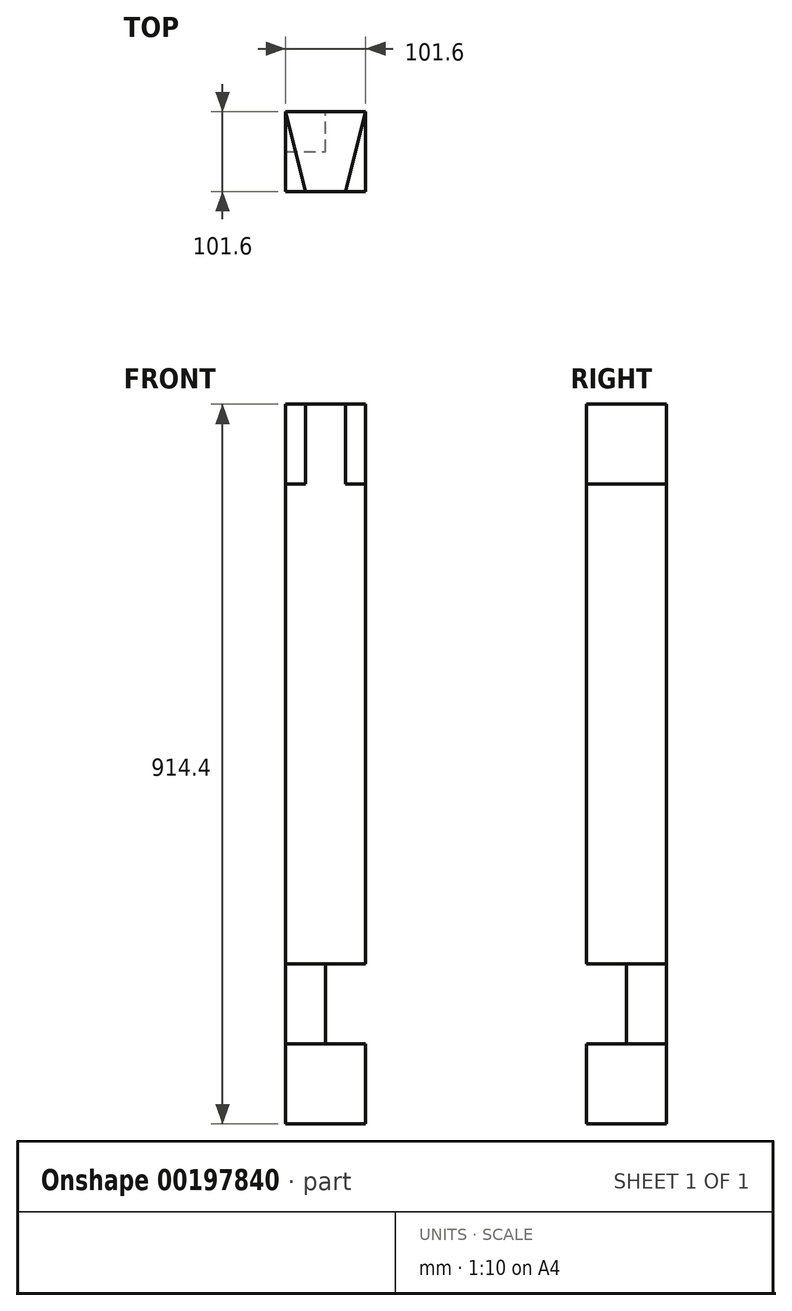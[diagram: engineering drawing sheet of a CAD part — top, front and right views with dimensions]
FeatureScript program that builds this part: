
annotation { "Feature Type Name" : "Feature", "Feature Type Description" : "" }
export const myFeature = defineFeature(function(context is Context, id is Id, definition is map)
    precondition{}
    {
        {
            var Q0;
            Q0=qCreatedBy(makeId("Top.planeOp"),FACE);
            var sketch = newSketch(context, id + "F0", { "sketchPlane" : qUnion([Q0])});
            skLineSegment(sketch, "E0.bottom", {"start": v(50.8, -50.8) * mm, "end": v(-50.8, -50.8) * mm});
            skLineSegment(sketch, "E0.top", {"start": v(50.8, 50.8) * mm, "end": v(-50.8, 50.8) * mm});
            skLineSegment(sketch, "E0.left", {"start": v(50.8, -50.8) * mm, "end": v(50.8, 50.8) * mm});
            skLineSegment(sketch, "E0.right", {"start": v(-50.8, -50.8) * mm, "end": v(-50.8, 50.8) * mm});
            skPoint(sketch, "E0.middle", {"position": v(0, 0) * mm});
            skSolve(sketch);
        }
        {
            var Q0;
            Q0=makeQuery(id+"F0.imprint","IMPRINT",FACE,{"disambiguationData":[TD([[makeQuery(id+"F0.imprint","IMPRINT",EDGE,{"derivedFrom":sQuery(id+"F0.wireOp",EDGE,"E0.bottom")}),-1.0]])]});
            extrude(context, id + "F1", {"entities" : qUnion([Q0]), "depth" : 914.4 * mm});
        }
        {
            var Q0;
            Q0=makeQuery(id+"F1.opExtrude","CAP_FACE",FACE,{"disambiguationData":[OSD([sQuery(id+"F0.wireOp",EDGE,"E0.bottom"),sQuery(id+"F0.wireOp",EDGE,"E0.top"),sQuery(id+"F0.wireOp",EDGE,"E0.left"),sQuery(id+"F0.wireOp",EDGE,"E0.right")])],"isStart":false});
            var sketch = newSketch(context, id + "F2", { "sketchPlane" : qUnion([Q0])});
            skLineSegment(sketch, "E1", {"start": v(-50.8, 50.8) * mm, "end": v(-25.4, -50.8) * mm});
            skLineSegment(sketch, "E2", {"start": v(0, 50.8) * mm, "end": v(0, -50.8) * mm, "construction": true});
            skLineSegment(sketch, "E3.MirrorCS", {"start": v(50.8, 50.8) * mm, "end": v(25.4, -50.8) * mm});
            skLineSegment(sketch, "E4", {"start": v(-50.8, 50.8) * mm, "end": v(50.8, 50.8) * mm});
            skLineSegment(sketch, "E5", {"start": v(25.4, -50.8) * mm, "end": v(-25.4, -50.8) * mm});
            skSolve(sketch);
        }
        {
            var Q0;
            {var subQ0=sQuery(id+"F2.wireOp",EDGE,"E1");Q0=makeQuery(id+"F2.imprint","IMPRINT",FACE,{"disambiguationData":[TD([[makeQuery(id+"F2.imprint","IMPRINT",EDGE,{"derivedFrom":subQ0}),-1.0]])]});}
            var Q1;
            {var subQ0=sQuery(id+"F2.wireOp",EDGE,"E3.MirrorCS");Q1=makeQuery(id+"F2.imprint","IMPRINT",FACE,{"disambiguationData":[TD([[makeQuery(id+"F2.imprint","IMPRINT",EDGE,{"derivedFrom":subQ0}),1.0]])]});}
            extrude(context, id + "F3", {"entities" : qUnion([Q0, Q1]), "operationType" : NewBodyOperationType.REMOVE, "oppositeDirection" : true, "depth" : 101.6 * mm});
        }
        {
            var Q0;
            Q0=makeQuery(id+"F1.opExtrude","SWEPT_FACE",FACE,{"disambiguationData":[OSD([sQuery(id+"F0.wireOp",EDGE,"E0.bottom")])]});
            var sketch = newSketch(context, id + "F4", { "sketchPlane" : qUnion([Q0])});
            skLineSegment(sketch, "E6.bottom", {"start": v(-50.8, 203.2) * mm, "end": v(50.8, 203.2) * mm});
            skLineSegment(sketch, "E6.top", {"start": v(-50.8, 101.6) * mm, "end": v(50.8, 101.6) * mm});
            skLineSegment(sketch, "E6.left", {"start": v(-50.8, 203.2) * mm, "end": v(-50.8, 101.6) * mm});
            skLineSegment(sketch, "E6.right", {"start": v(50.8, 203.2) * mm, "end": v(50.8, 101.6) * mm});
            skSolve(sketch);
        }
        {
            var Q0;
            Q0=makeQuery(id+"F4.imprint","IMPRINT",FACE,{"disambiguationData":[TD([[makeQuery(id+"F4.imprint","IMPRINT",EDGE,{"derivedFrom":sQuery(id+"F4.wireOp",EDGE,"E6.bottom")}),-1.0]])]});
            extrude(context, id + "F5", {"entities" : qUnion([Q0]), "operationType" : NewBodyOperationType.REMOVE, "oppositeDirection" : true, "depth" : 50.8 * mm});
        }
        {
            var Q0;
            Q0=makeQuery(id+"F1.opExtrude","SWEPT_FACE",FACE,{"disambiguationData":[OSD([sQuery(id+"F0.wireOp",EDGE,"E0.left")])]});
            var sketch = newSketch(context, id + "F6", { "sketchPlane" : qUnion([Q0])});
            skLineSegment(sketch, "E7.bottom", {"start": v(-50.8, 203.2) * mm, "end": v(50.8, 203.2) * mm});
            skLineSegment(sketch, "E7.top", {"start": v(-50.8, 101.6) * mm, "end": v(50.8, 101.6) * mm});
            skLineSegment(sketch, "E7.left", {"start": v(-50.8, 203.2) * mm, "end": v(-50.8, 101.6) * mm});
            skLineSegment(sketch, "E7.right", {"start": v(50.8, 203.2) * mm, "end": v(50.8, 101.6) * mm});
            skSolve(sketch);
        }
        {
            var Q0;
            Q0=makeQuery(id+"F6.imprint","IMPRINT",FACE,{"disambiguationData":[TD([[makeQuery(id+"F6.imprint","IMPRINT",EDGE,{"derivedFrom":sQuery(id+"F6.wireOp",EDGE,"E7.bottom")}),-1.0]])]});
            extrude(context, id + "F7", {"entities" : qUnion([Q0]), "operationType" : NewBodyOperationType.REMOVE, "oppositeDirection" : true, "depth" : 50.8 * mm});
        }
    });
